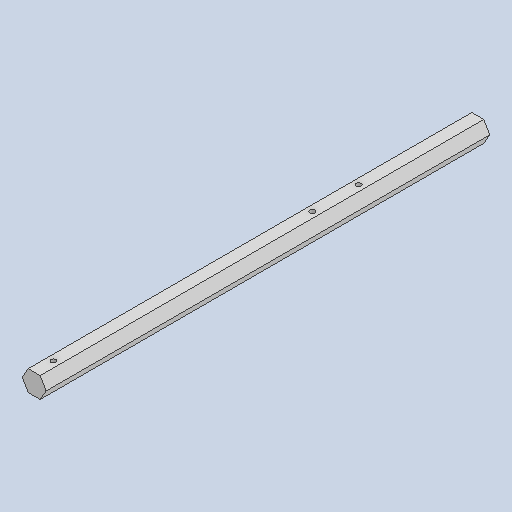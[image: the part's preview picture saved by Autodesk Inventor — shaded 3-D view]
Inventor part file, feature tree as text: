
AUTODESK INVENTOR PART (.ipt)
format: ipt  version: 2022 (Build 260153000, 153)  size: 121,856 bytes
history: native  units: mm
features: extrude x2, sketch x2
ambient origin geometry x8: Origin, YZ Plane, XZ Plane, XY Plane, X Axis, Y Axis, Z Axis, Center Point
bodies: Body1 (feature_tree)
feature tree (4):
  extrude  "Extrusion6"  Depth=3.1mm TaperAngle=360.0deg
  extrude  "Extrusion7"  Depth=115.0mm
  sketch  "Sketch4"  dims[d21=3.1mm d22=60.0mm d24=360.0deg]
  sketch  "Sketch5"  dims[d26=115.0mm d27=0.0mm d28=1.3mm d29=84.1mm d30=72.1mm d31=5.0mm d32=6.0mm d33=0.0mm]
